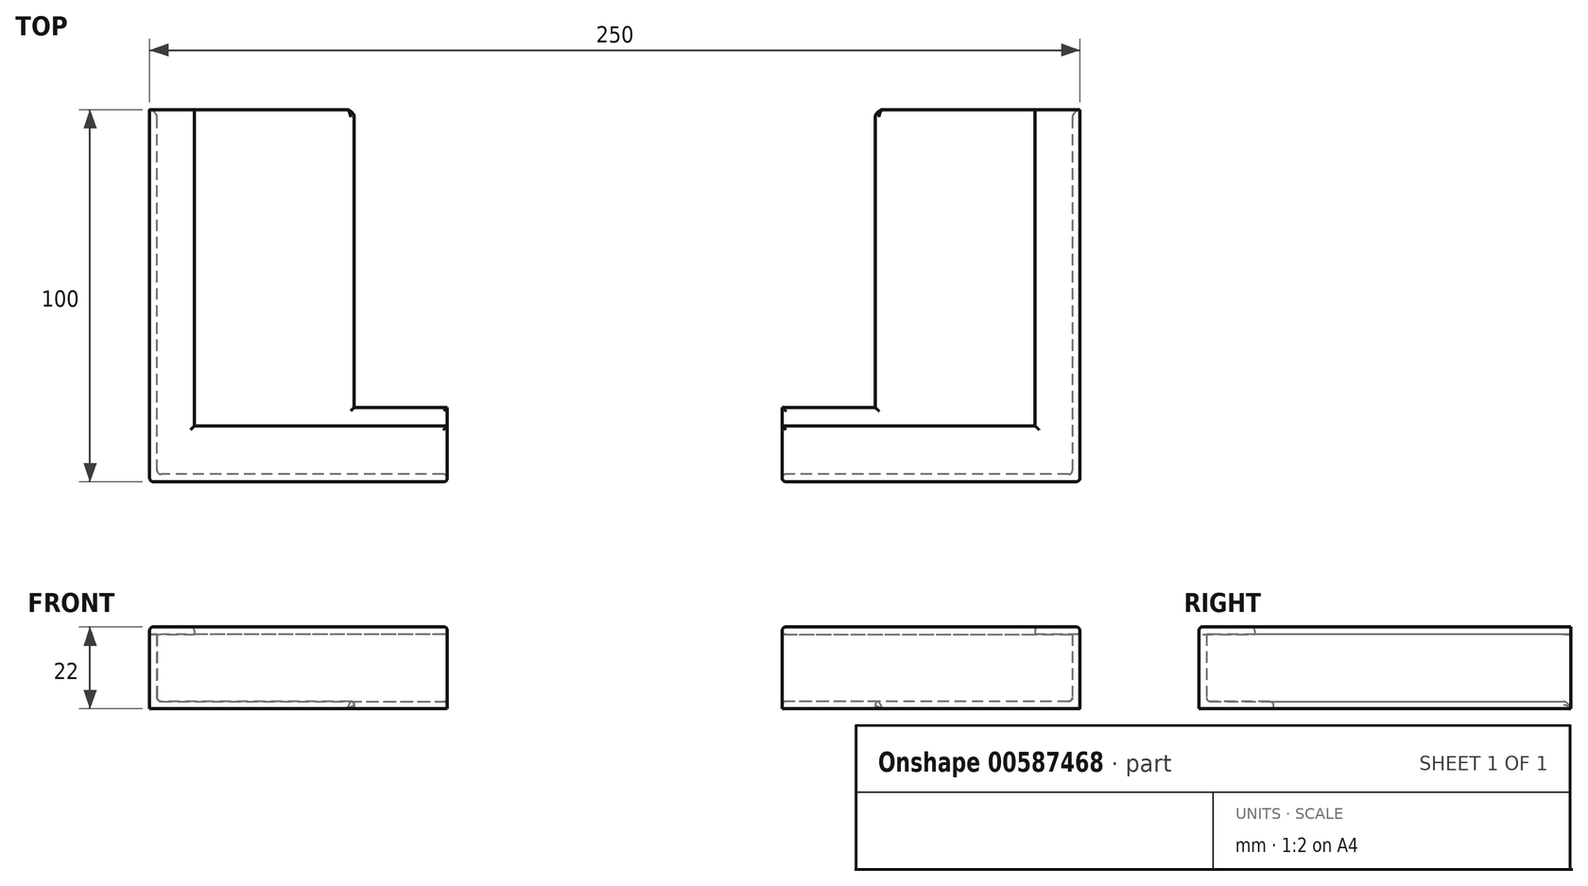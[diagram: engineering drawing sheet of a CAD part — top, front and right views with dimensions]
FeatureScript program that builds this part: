
annotation { "Feature Type Name" : "Feature", "Feature Type Description" : "" }
export const myFeature = defineFeature(function(context is Context, id is Id, definition is map)
    precondition{}
    {
        {
            var Q0;
            Q0=qCreatedBy(makeId("Top.planeOp"),FACE);
            var sketch = newSketch(context, id + "F0", { "sketchPlane" : qUnion([Q0])});
            skLineSegment(sketch, "E0.bottom", {"start": v(-125, 50) * mm, "end": v(-45, 50) * mm});
            skLineSegment(sketch, "E0.top", {"start": v(-125, -50) * mm, "end": v(-45, -50) * mm});
            skLineSegment(sketch, "E0.left", {"start": v(-125, 50) * mm, "end": v(-125, -50) * mm});
            skLineSegment(sketch, "E0.right", {"start": v(-45, 50) * mm, "end": v(-45, -50) * mm});
            skPoint(sketch, "E1.oppositeSnap0", {"position": v(-85, 50) * mm});
            skLineSegment(sketch, "E1.bottom", {"start": v(45, -50) * mm, "end": v(125, -50) * mm});
            skLineSegment(sketch, "E1.top", {"start": v(45, 50) * mm, "end": v(125, 50) * mm});
            skLineSegment(sketch, "E1.left", {"start": v(45, -50) * mm, "end": v(45, 50) * mm});
            skLineSegment(sketch, "E1.right", {"start": v(125, -50) * mm, "end": v(125, 50) * mm});
            skSolve(sketch);
        }
        {
            var Q0;
            Q0 = qSketchRegion(id + "F0", true);
            extrude(context, id + "F1", {"entities" : qUnion([Q0]), "depth" : 2 * mm, "offsetDistance" : 25 * mm});
        }
        {
            var Q0;
            Q0=qCreatedBy(makeId("Top.planeOp"),FACE);
            var sketch = newSketch(context, id + "F2", { "sketchPlane" : qUnion([Q0])});
            skLineSegment(sketch, "E2.0", {"start": v(-125, 50) * mm, "end": v(-125, -50) * mm});
            skLineSegment(sketch, "E2.1", {"start": v(-125, -50) * mm, "end": v(-45, -50) * mm});
            skLineSegment(sketch, "E2.2", {"start": v(45, -50) * mm, "end": v(125, -50) * mm});
            skLineSegment(sketch, "E2.3", {"start": v(125, -50) * mm, "end": v(125, 50) * mm});
            skLineSegment(sketch, "E3.bottom", {"start": v(-125, 50) * mm, "end": v(-123, 50) * mm});
            skLineSegment(sketch, "E3.top", {"start": v(-125, -50) * mm, "end": v(-123, -50) * mm});
            skLineSegment(sketch, "E3.right", {"start": v(-123, 50) * mm, "end": v(-123, -50) * mm});
            skLineSegment(sketch, "E4.bottom", {"start": v(-45, -50) * mm, "end": v(-125, -50) * mm});
            skLineSegment(sketch, "E4.top", {"start": v(-45, -48) * mm, "end": v(-125, -48) * mm});
            skLineSegment(sketch, "E4.left", {"start": v(-45, -50) * mm, "end": v(-45, -48) * mm});
            skLineSegment(sketch, "E4.right", {"start": v(-125, -50) * mm, "end": v(-125, -48) * mm});
            skLineSegment(sketch, "E5.top", {"start": v(45, -48) * mm, "end": v(125, -48) * mm});
            skLineSegment(sketch, "E5.left", {"start": v(45, -50) * mm, "end": v(45, -48) * mm});
            skLineSegment(sketch, "E5.right", {"start": v(125, -50) * mm, "end": v(125, -48) * mm});
            skLineSegment(sketch, "E6.bottom", {"start": v(125, 50) * mm, "end": v(123, 50) * mm});
            skLineSegment(sketch, "E6.top", {"start": v(125, -50) * mm, "end": v(123, -50) * mm});
            skLineSegment(sketch, "E6.left", {"start": v(125, 50) * mm, "end": v(125, -50) * mm});
            skLineSegment(sketch, "E6.right", {"start": v(123, 50) * mm, "end": v(123, -50) * mm});
            skSolve(sketch);
        }
        {
            var Q0;
            Q0 = qSketchRegion(id + "F2", true);
            extrude(context, id + "F3", {"entities" : qUnion([Q0]), "operationType" : NewBodyOperationType.ADD, "depth" : 20 * mm, "offsetDistance" : 25 * mm});
        }
        {
            var Q0;
            Q0=makeQuery(id+"F3.opExtrude","CAP_FACE",FACE,{"disambiguationData":[OSD([sQuery(id+"F2.wireOp",EDGE,"E3.bottom"),sQuery(id+"F2.wireOp",EDGE,"E2.0"),sQuery(id+"F2.wireOp",EDGE,"E3.right"),sQuery(id+"F2.wireOp",EDGE,"E4.bottom"),sQuery(id+"F2.wireOp",EDGE,"E4.top"),sQuery(id+"F2.wireOp",EDGE,"E4.left"),sQuery(id+"F2.wireOp",EDGE,"E4.right")])],"isStart":false});
            var sketch = newSketch(context, id + "F4", { "sketchPlane" : qUnion([Q0])});
            skLineSegment(sketch, "E7.0", {"start": v(-125, 50) * mm, "end": v(-125, -50) * mm});
            skLineSegment(sketch, "E7.1", {"start": v(-45, -50) * mm, "end": v(-125, -50) * mm});
            skLineSegment(sketch, "E7.2", {"start": v(45, -50) * mm, "end": v(125, -50) * mm});
            skLineSegment(sketch, "E7.3", {"start": v(125, 50) * mm, "end": v(125, -50) * mm});
            skLineSegment(sketch, "E8.bottom", {"start": v(-125, 50) * mm, "end": v(-113, 50) * mm});
            skLineSegment(sketch, "E8.top", {"start": v(-125, -50) * mm, "end": v(-113, -50) * mm});
            skLineSegment(sketch, "E8.right", {"start": v(-113, 50) * mm, "end": v(-113, -35) * mm});
            skLineSegment(sketch, "E9.bottom", {"start": v(125, 50) * mm, "end": v(113, 50) * mm});
            skLineSegment(sketch, "E9.top", {"start": v(125, -50) * mm, "end": v(113, -50) * mm});
            skLineSegment(sketch, "E9.right", {"start": v(113, 50) * mm, "end": v(113, -35) * mm});
            skLineSegment(sketch, "E10.top", {"start": v(45, -35) * mm, "end": v(113, -35) * mm});
            skLineSegment(sketch, "E10.left", {"start": v(45, -50) * mm, "end": v(45, -35) * mm});
            skLineSegment(sketch, "E10.right", {"start": v(125, -50) * mm, "end": v(125, -35) * mm});
            skLineSegment(sketch, "E11.top", {"start": v(-45, -35) * mm, "end": v(-113, -35) * mm});
            skLineSegment(sketch, "E11.left", {"start": v(-45, -50) * mm, "end": v(-45, -35) * mm});
            skLineSegment(sketch, "E11.right", {"start": v(-125, -50) * mm, "end": v(-125, -35) * mm});
            skSolve(sketch);
        }
        {
            var Q0;
            Q0 = qSketchRegion(id + "F4", true);
            extrude(context, id + "F5", {"entities" : qUnion([Q0]), "operationType" : NewBodyOperationType.ADD, "depth" : 2 * mm, "offsetDistance" : 25 * mm});
        }
        {
            var Q0;
            Q0=makeQuery(id+"F3.boolean.opBoolean","INTERSECT",EDGE,{"derivedFrom":[makeQuery(id+"F1.opExtrude","CAP_FACE",FACE,{"disambiguationData":[OSD([sQuery(id+"F0.wireOp",EDGE,"E0.bottom"),sQuery(id+"F0.wireOp",EDGE,"E0.top"),sQuery(id+"F0.wireOp",EDGE,"E0.left"),sQuery(id+"F0.wireOp",EDGE,"E0.right")])],"isStart":false}),makeQuery(id+"F3.opExtrude","SWEPT_FACE",FACE,{"disambiguationData":[OSD([sQuery(id+"F2.wireOp",EDGE,"E3.right")])]})]});
            var Q1;
            Q1=makeQuery(id+"F3.boolean.opBoolean","INTERSECT",EDGE,{"derivedFrom":[makeQuery(id+"F1.opExtrude","CAP_FACE",FACE,{"disambiguationData":[OSD([sQuery(id+"F0.wireOp",EDGE,"E0.bottom"),sQuery(id+"F0.wireOp",EDGE,"E0.top"),sQuery(id+"F0.wireOp",EDGE,"E0.left"),sQuery(id+"F0.wireOp",EDGE,"E0.right")])],"isStart":false}),makeQuery(id+"F3.opExtrude","SWEPT_FACE",FACE,{"disambiguationData":[OSD([sQuery(id+"F2.wireOp",EDGE,"E4.top")])]})]});
            var Q2;
            Q2=makeQuery(id+"F3.opExtrude","SWEPT_EDGE",EDGE,{"disambiguationData":[OSD([sQuery(id+"F2.wireOp",EDGE,"E3.right"),sQuery(id+"F2.wireOp",EDGE,"E4.top")])]});
            var Q3;
            Q3=makeQuery(id+"F3.opExtrude","CAP_EDGE",EDGE,{"disambiguationData":[OSD([sQuery(id+"F2.wireOp",EDGE,"E3.right")])],"isStart":false});
            var Q4;
            Q4=makeQuery(id+"F3.opExtrude","CAP_EDGE",EDGE,{"disambiguationData":[OSD([sQuery(id+"F2.wireOp",EDGE,"E4.top")])],"isStart":false});
            var Q5;
            Q5=makeQuery(id+"F5.opExtrude","CAP_EDGE",EDGE,{"disambiguationData":[OSD([sQuery(id+"F4.wireOp",EDGE,"E7.1")])],"isStart":false});
            var Q6;
            Q6=makeQuery(id+"F5.opExtrude","CAP_EDGE",EDGE,{"disambiguationData":[OSD([sQuery(id+"F4.wireOp",EDGE,"E7.0"),sQuery(id+"F4.wireOp",EDGE,"E11.right")])],"isStart":false});
            var Q7;
            Q7=makeQuery(id+"F5.boolean.opBoolean","MERGE",EDGE,{"derivedFrom":[makeQuery(id+"F3.boolean.opBoolean","MERGE",EDGE,{"derivedFrom":[makeQuery(id+"F1.opExtrude","SWEPT_EDGE",EDGE,{"disambiguationData":[OSD([sQuery(id+"F0.wireOp",EDGE,"E0.top"),sQuery(id+"F0.wireOp",EDGE,"E0.left")])]}),makeQuery(id+"F3.opExtrude","SWEPT_EDGE",EDGE,{"disambiguationData":[OSD([sQuery(id+"F2.wireOp",EDGE,"E4.bottom"),sQuery(id+"F2.wireOp",EDGE,"E4.right")])]})]}),makeQuery(id+"F5.opExtrude","SWEPT_EDGE",EDGE,{"disambiguationData":[OSD([sQuery(id+"F4.wireOp",EDGE,"E7.1"),sQuery(id+"F4.wireOp",EDGE,"E11.right")])]})]});
            var Q8;
            Q8=makeQuery(id+"F5.opExtrude","CAP_EDGE",EDGE,{"disambiguationData":[OSD([sQuery(id+"F4.wireOp",EDGE,"E7.2")])],"isStart":false});
            var Q9;
            Q9=makeQuery(id+"F5.opExtrude","CAP_EDGE",EDGE,{"disambiguationData":[OSD([sQuery(id+"F4.wireOp",EDGE,"E7.3"),sQuery(id+"F4.wireOp",EDGE,"E10.right")])],"isStart":false});
            var Q10;
            Q10=makeQuery(id+"F5.boolean.opBoolean","MERGE",EDGE,{"derivedFrom":[makeQuery(id+"F3.boolean.opBoolean","MERGE",EDGE,{"derivedFrom":[makeQuery(id+"F1.opExtrude","SWEPT_EDGE",EDGE,{"disambiguationData":[OSD([sQuery(id+"F0.wireOp",EDGE,"E1.bottom"),sQuery(id+"F0.wireOp",EDGE,"E1.right")])]}),makeQuery(id+"F3.opExtrude","SWEPT_EDGE",EDGE,{"disambiguationData":[OSD([sQuery(id+"F2.wireOp",EDGE,"E6.top"),sQuery(id+"F2.wireOp",EDGE,"E6.left")])]})]}),makeQuery(id+"F5.opExtrude","SWEPT_EDGE",EDGE,{"disambiguationData":[OSD([sQuery(id+"F4.wireOp",EDGE,"E7.2"),sQuery(id+"F4.wireOp",EDGE,"E10.right")])]})]});
            var Q11;
            Q11=makeQuery(id+"F3.boolean.opBoolean","INTERSECT",EDGE,{"derivedFrom":[makeQuery(id+"F1.opExtrude","CAP_FACE",FACE,{"disambiguationData":[OSD([sQuery(id+"F0.wireOp",EDGE,"E1.bottom"),sQuery(id+"F0.wireOp",EDGE,"E1.top"),sQuery(id+"F0.wireOp",EDGE,"E1.left"),sQuery(id+"F0.wireOp",EDGE,"E1.right")])],"isStart":false}),makeQuery(id+"F3.opExtrude","SWEPT_FACE",FACE,{"disambiguationData":[OSD([sQuery(id+"F2.wireOp",EDGE,"E6.right")])]})]});
            var Q12;
            Q12=makeQuery(id+"F3.boolean.opBoolean","INTERSECT",EDGE,{"derivedFrom":[makeQuery(id+"F1.opExtrude","CAP_FACE",FACE,{"disambiguationData":[OSD([sQuery(id+"F0.wireOp",EDGE,"E1.bottom"),sQuery(id+"F0.wireOp",EDGE,"E1.top"),sQuery(id+"F0.wireOp",EDGE,"E1.left"),sQuery(id+"F0.wireOp",EDGE,"E1.right")])],"isStart":false}),makeQuery(id+"F3.opExtrude","SWEPT_FACE",FACE,{"disambiguationData":[OSD([sQuery(id+"F2.wireOp",EDGE,"E5.top")])]})]});
            var Q13;
            Q13=makeQuery(id+"F3.opExtrude","CAP_EDGE",EDGE,{"disambiguationData":[OSD([sQuery(id+"F2.wireOp",EDGE,"E5.top")])],"isStart":false});
            var Q14;
            Q14=makeQuery(id+"F3.opExtrude","CAP_EDGE",EDGE,{"disambiguationData":[OSD([sQuery(id+"F2.wireOp",EDGE,"E6.right")])],"isStart":false});
            var Q15;
            Q15=makeQuery(id+"F3.opExtrude","SWEPT_EDGE",EDGE,{"disambiguationData":[OSD([sQuery(id+"F2.wireOp",EDGE,"E5.top"),sQuery(id+"F2.wireOp",EDGE,"E6.right")])]});
            fillet(context, id + "F6", {"entities" : qUnion([Q0, Q1, Q2, Q3, Q4, Q5, Q6, Q7, Q8, Q9, Q10, Q11, Q12, Q13, Q14, Q15]), "radius" : 1 * mm, "tangentPropagation" : true, "allowEdgeOverflow" : false});
        }
        {
            var Q0;
            Q0=makeQuery(id+"F1.opExtrude","CAP_FACE",FACE,{"disambiguationData":[OSD([sQuery(id+"F0.wireOp",EDGE,"E0.bottom"),sQuery(id+"F0.wireOp",EDGE,"E0.top"),sQuery(id+"F0.wireOp",EDGE,"E0.left"),sQuery(id+"F0.wireOp",EDGE,"E0.right")])],"isStart":true});
            var sketch = newSketch(context, id + "F7", { "sketchPlane" : qUnion([Q0])});
            skLineSegment(sketch, "E12.bottom", {"start": v(-45, -50) * mm, "end": v(-70, -50) * mm});
            skLineSegment(sketch, "E12.top", {"start": v(-45, 30) * mm, "end": v(-70, 30) * mm});
            skLineSegment(sketch, "E12.left", {"start": v(-45, -50) * mm, "end": v(-45, 30) * mm});
            skLineSegment(sketch, "E12.right", {"start": v(-70, -50) * mm, "end": v(-70, 30) * mm});
            skPoint(sketch, "E13.0", {"position": v(45, -50) * mm});
            skLineSegment(sketch, "E14.bottom", {"start": v(45, -50) * mm, "end": v(70, -50) * mm});
            skLineSegment(sketch, "E14.top", {"start": v(45, 30) * mm, "end": v(70, 30) * mm});
            skLineSegment(sketch, "E14.left", {"start": v(45, -50) * mm, "end": v(45, 30) * mm});
            skLineSegment(sketch, "E14.right", {"start": v(70, -50) * mm, "end": v(70, 30) * mm});
            skSolve(sketch);
        }
        {
            var Q0;
            Q0 = qSketchRegion(id + "F7", true);
            extrude(context, id + "F8", {"entities" : qUnion([Q0]), "operationType" : NewBodyOperationType.REMOVE, "endBound" : BoundingType.THROUGH_ALL, "oppositeDirection" : true, "depth" : 25 * mm, "offsetDistance" : 25 * mm});
        }
        {
            var Q0;
            Q0=makeQuery(id+"F8.boolean.opBoolean","INTERSECT",EDGE,{"derivedFrom":[makeQuery(id+"F1.opExtrude","CAP_FACE",FACE,{"disambiguationData":[OSD([sQuery(id+"F0.wireOp",EDGE,"E0.bottom"),sQuery(id+"F0.wireOp",EDGE,"E0.top"),sQuery(id+"F0.wireOp",EDGE,"E0.left"),sQuery(id+"F0.wireOp",EDGE,"E0.right")])],"isStart":false}),makeQuery(id+"F8.opExtrude","SWEPT_FACE",FACE,{"disambiguationData":[OSD([sQuery(id+"F7.wireOp",EDGE,"E12.right")])]})]});
            var Q1;
            Q1=makeQuery(id+"F8.boolean.opBoolean","INTERSECT",EDGE,{"derivedFrom":[makeQuery(id+"F1.opExtrude","CAP_FACE",FACE,{"disambiguationData":[OSD([sQuery(id+"F0.wireOp",EDGE,"E1.bottom"),sQuery(id+"F0.wireOp",EDGE,"E1.top"),sQuery(id+"F0.wireOp",EDGE,"E1.left"),sQuery(id+"F0.wireOp",EDGE,"E1.right")])],"isStart":false}),makeQuery(id+"F8.opExtrude","SWEPT_FACE",FACE,{"disambiguationData":[OSD([sQuery(id+"F7.wireOp",EDGE,"E14.right")])]})]});
            var Q2;
            Q2=makeQuery(id+"F8.boolean.opBoolean","INTERSECT",EDGE,{"derivedFrom":[makeQuery(id+"F1.opExtrude","CAP_FACE",FACE,{"disambiguationData":[OSD([sQuery(id+"F0.wireOp",EDGE,"E1.bottom"),sQuery(id+"F0.wireOp",EDGE,"E1.top"),sQuery(id+"F0.wireOp",EDGE,"E1.left"),sQuery(id+"F0.wireOp",EDGE,"E1.right")])],"isStart":false}),makeQuery(id+"F8.opExtrude","SWEPT_FACE",FACE,{"disambiguationData":[OSD([sQuery(id+"F7.wireOp",EDGE,"E14.top")])]})]});
            var Q3;
            Q3=makeQuery(id+"F8.boolean.opBoolean","INTERSECT",EDGE,{"derivedFrom":[makeQuery(id+"F1.opExtrude","CAP_FACE",FACE,{"disambiguationData":[OSD([sQuery(id+"F0.wireOp",EDGE,"E0.bottom"),sQuery(id+"F0.wireOp",EDGE,"E0.top"),sQuery(id+"F0.wireOp",EDGE,"E0.left"),sQuery(id+"F0.wireOp",EDGE,"E0.right")])],"isStart":false}),makeQuery(id+"F8.opExtrude","SWEPT_FACE",FACE,{"disambiguationData":[OSD([sQuery(id+"F7.wireOp",EDGE,"E12.top")])]})]});
            var Q4;
            Q4=makeQuery(id+"F1.opExtrude","CAP_EDGE",EDGE,{"disambiguationData":[OSD([sQuery(id+"F0.wireOp",EDGE,"E0.right")])],"isStart":false});
            var Q5;
            Q5=makeQuery(id+"F5.opExtrude","CAP_EDGE",EDGE,{"disambiguationData":[OSD([sQuery(id+"F4.wireOp",EDGE,"E8.right")])],"isStart":false});
            var Q6;
            Q6=makeQuery(id+"F5.opExtrude","CAP_EDGE",EDGE,{"disambiguationData":[OSD([sQuery(id+"F4.wireOp",EDGE,"E11.top")])],"isStart":false});
            var Q7;
            Q7=makeQuery(id+"F5.opExtrude","CAP_EDGE",EDGE,{"disambiguationData":[OSD([sQuery(id+"F4.wireOp",EDGE,"E10.top")])],"isStart":false});
            var Q8;
            Q8=makeQuery(id+"F5.opExtrude","CAP_EDGE",EDGE,{"disambiguationData":[OSD([sQuery(id+"F4.wireOp",EDGE,"E9.right")])],"isStart":false});
            var Q9;
            Q9=makeQuery(id+"F1.opExtrude","CAP_EDGE",EDGE,{"disambiguationData":[OSD([sQuery(id+"F0.wireOp",EDGE,"E1.left")])],"isStart":false});
            var Q10;
            Q10=makeQuery(id+"F5.opExtrude","CAP_EDGE",EDGE,{"disambiguationData":[OSD([sQuery(id+"F4.wireOp",EDGE,"E11.left")])],"isStart":false});
            var Q11;
            Q11=makeQuery(id+"F5.opExtrude","CAP_EDGE",EDGE,{"disambiguationData":[OSD([sQuery(id+"F4.wireOp",EDGE,"E10.left")])],"isStart":false});
            fillet(context, id + "F9", {"entities" : qUnion([Q0, Q1, Q2, Q3, Q4, Q5, Q6, Q7, Q8, Q9, Q10, Q11]), "radius" : 1 * mm, "tangentPropagation" : true, "allowEdgeOverflow" : false});
        }
        {
            var Q0;
            Q0=makeQuery(id+"F1.opExtrude","CAP_EDGE",EDGE,{"disambiguationData":[OSD([sQuery(id+"F0.wireOp",EDGE,"E1.top")])],"isStart":false});
            var Q1;
            Q1=makeQuery(id+"F1.opExtrude","CAP_EDGE",EDGE,{"disambiguationData":[OSD([sQuery(id+"F0.wireOp",EDGE,"E0.bottom")])],"isStart":false});
            fillet(context, id + "F10", {"entities" : qUnion([Q0, Q1]), "radius" : 2 * mm, "tangentPropagation" : true, "rho" : 0.3, "crossSection" : FilletCrossSection.CONIC, "allowEdgeOverflow" : false});
        }
    });
